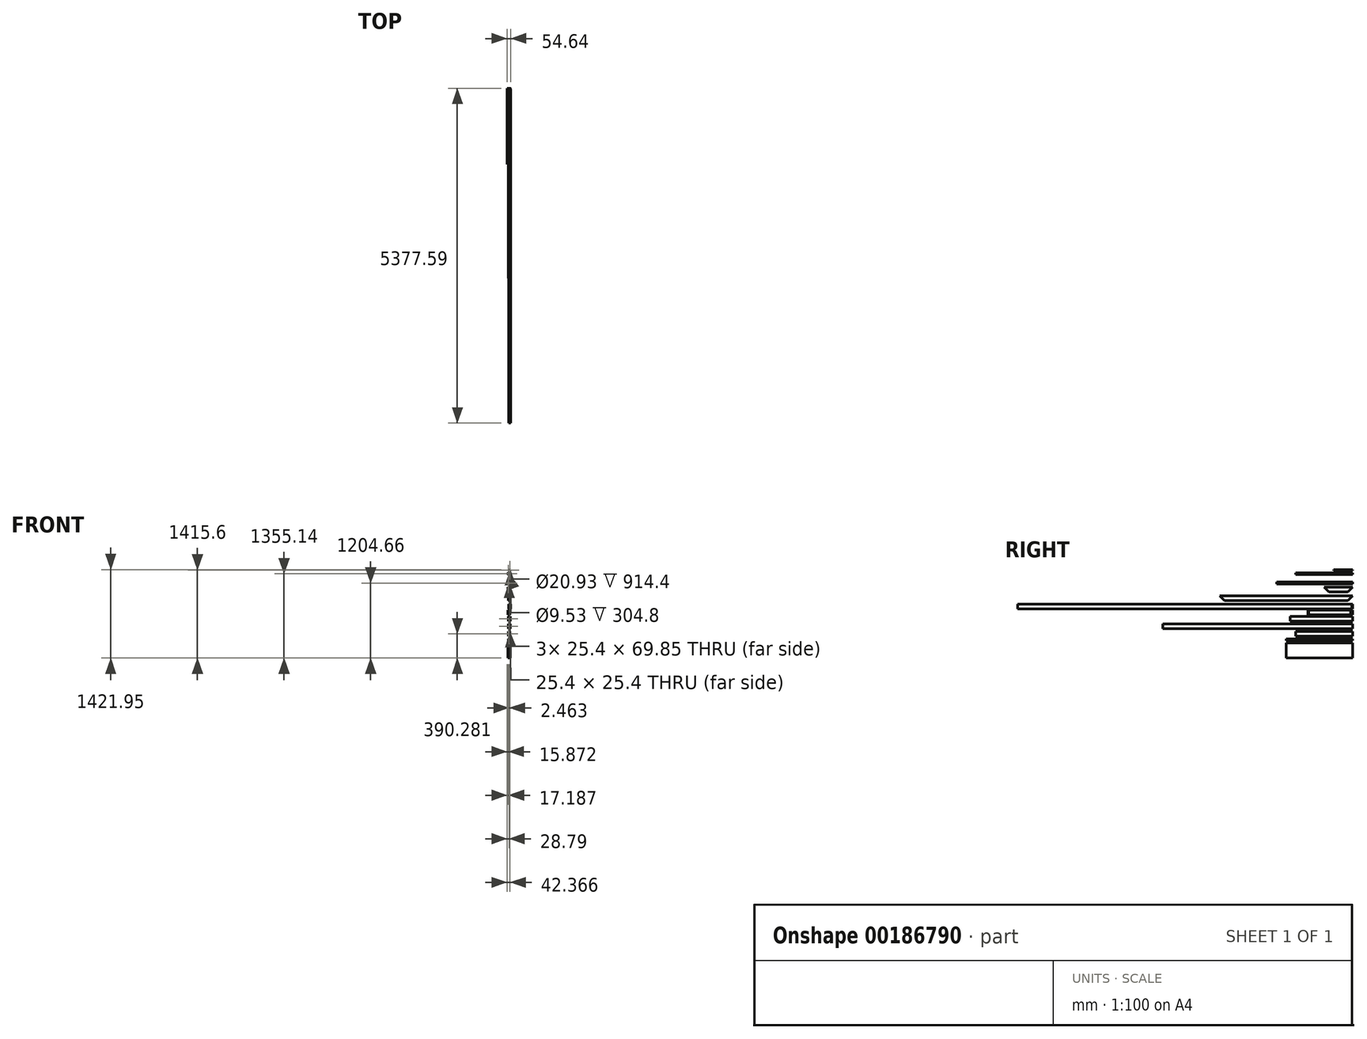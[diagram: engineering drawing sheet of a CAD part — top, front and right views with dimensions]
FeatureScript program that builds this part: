
annotation { "Feature Type Name" : "Feature", "Feature Type Description" : "" }
export const myFeature = defineFeature(function(context is Context, id is Id, definition is map)
    precondition{}
    {
        {
            var Q0;
            Q0=qCreatedBy(makeId("Front.planeOp"),FACE);
            var sketch = newSketch(context, id + "F0", { "sketchPlane" : qUnion([Q0])});
            skLineSegment(sketch, "E0.bottom", {"start": v(-82.17, 96.46) * mm, "end": v(-56.77, 96.46) * mm});
            skLineSegment(sketch, "E0.top", {"start": v(-82.17, 26.61) * mm, "end": v(-56.77, 26.61) * mm});
            skLineSegment(sketch, "E0.left", {"start": v(-82.17, 96.46) * mm, "end": v(-82.17, 26.61) * mm});
            skLineSegment(sketch, "E0.right", {"start": v(-56.77, 96.46) * mm, "end": v(-56.77, 26.61) * mm});
            skLineSegment(sketch, "E1.bottom", {"start": v(-85.35, 99.64) * mm, "end": v(-53.6, 99.64) * mm});
            skLineSegment(sketch, "E1.top", {"start": v(-85.35, 23.44) * mm, "end": v(-53.6, 23.44) * mm});
            skLineSegment(sketch, "E1.left", {"start": v(-85.35, 99.64) * mm, "end": v(-85.35, 23.44) * mm});
            skLineSegment(sketch, "E1.right", {"start": v(-53.6, 99.64) * mm, "end": v(-53.6, 23.44) * mm});
            skLineSegment(sketch, "E2.bottom", {"start": v(-92.32, -2.1) * mm, "end": v(-66.92, -2.1) * mm});
            skLineSegment(sketch, "E2.top", {"start": v(-92.32, -71.95) * mm, "end": v(-66.92, -71.95) * mm});
            skLineSegment(sketch, "E2.left", {"start": v(-92.32, -2.1) * mm, "end": v(-92.32, -71.95) * mm});
            skLineSegment(sketch, "E2.right", {"start": v(-66.92, -2.1) * mm, "end": v(-66.92, -71.95) * mm});
            skLineSegment(sketch, "E3.bottom", {"start": v(-95.5, 1.08) * mm, "end": v(-63.75, 1.08) * mm});
            skLineSegment(sketch, "E3.top", {"start": v(-95.5, -75.12) * mm, "end": v(-63.75, -75.12) * mm});
            skLineSegment(sketch, "E3.left", {"start": v(-95.5, 1.08) * mm, "end": v(-95.5, -75.12) * mm});
            skLineSegment(sketch, "E3.right", {"start": v(-63.75, 1.08) * mm, "end": v(-63.75, -75.12) * mm});
            skLineSegment(sketch, "E4.bottom", {"start": v(-87.37, -104.41) * mm, "end": v(-61.97, -104.41) * mm});
            skLineSegment(sketch, "E4.top", {"start": v(-87.37, -174.26) * mm, "end": v(-61.97, -174.26) * mm});
            skLineSegment(sketch, "E4.left", {"start": v(-87.37, -104.41) * mm, "end": v(-87.37, -174.26) * mm});
            skLineSegment(sketch, "E4.right", {"start": v(-61.97, -104.41) * mm, "end": v(-61.97, -174.26) * mm});
            skLineSegment(sketch, "E5.bottom", {"start": v(-90.55, -101.24) * mm, "end": v(-58.8, -101.24) * mm});
            skLineSegment(sketch, "E5.top", {"start": v(-90.55, -177.44) * mm, "end": v(-58.8, -177.44) * mm});
            skLineSegment(sketch, "E5.left", {"start": v(-90.55, -101.24) * mm, "end": v(-90.55, -177.44) * mm});
            skLineSegment(sketch, "E5.right", {"start": v(-58.8, -101.24) * mm, "end": v(-58.8, -177.44) * mm});
            skLineSegment(sketch, "E6.bottom", {"start": v(-89.69, -223.53) * mm, "end": v(-64.29, -223.53) * mm});
            skLineSegment(sketch, "E6.top", {"start": v(-89.69, -293.38) * mm, "end": v(-64.29, -293.38) * mm});
            skLineSegment(sketch, "E6.left", {"start": v(-89.69, -223.53) * mm, "end": v(-89.69, -293.38) * mm});
            skLineSegment(sketch, "E6.right", {"start": v(-64.29, -223.53) * mm, "end": v(-64.29, -293.38) * mm});
            skLineSegment(sketch, "E7.bottom", {"start": v(-92.86, -220.36) * mm, "end": v(-61.11, -220.36) * mm});
            skLineSegment(sketch, "E7.top", {"start": v(-92.86, -296.56) * mm, "end": v(-61.11, -296.56) * mm});
            skLineSegment(sketch, "E7.left", {"start": v(-92.86, -220.36) * mm, "end": v(-92.86, -296.56) * mm});
            skLineSegment(sketch, "E7.right", {"start": v(-61.11, -220.36) * mm, "end": v(-61.11, -296.56) * mm});
            skLineSegment(sketch, "E8.bottom", {"start": v(-92.15, -344.23) * mm, "end": v(-66.75, -344.23) * mm});
            skLineSegment(sketch, "E8.top", {"start": v(-92.15, -414.08) * mm, "end": v(-66.75, -414.08) * mm});
            skLineSegment(sketch, "E8.left", {"start": v(-92.15, -344.23) * mm, "end": v(-92.15, -414.08) * mm});
            skLineSegment(sketch, "E8.right", {"start": v(-66.75, -344.23) * mm, "end": v(-66.75, -414.08) * mm});
            skLineSegment(sketch, "E9.bottom", {"start": v(-95.33, -341.06) * mm, "end": v(-63.58, -341.06) * mm});
            skLineSegment(sketch, "E9.top", {"start": v(-95.33, -417.26) * mm, "end": v(-63.58, -417.26) * mm});
            skLineSegment(sketch, "E9.left", {"start": v(-95.33, -341.06) * mm, "end": v(-95.33, -417.26) * mm});
            skLineSegment(sketch, "E9.right", {"start": v(-63.58, -341.06) * mm, "end": v(-63.58, -417.26) * mm});
            skLineSegment(sketch, "E10", {"start": v(-95.36, -464.32) * mm, "end": v(-95.36, -489.72) * mm});
            skLineSegment(sketch, "E11", {"start": v(-95.36, -489.72) * mm, "end": v(-69.96, -489.72) * mm});
            skLineSegment(sketch, "E12", {"start": v(-69.96, -489.72) * mm, "end": v(-69.96, -486.54) * mm});
            skLineSegment(sketch, "E13", {"start": v(-69.96, -486.54) * mm, "end": v(-92.19, -486.54) * mm});
            skLineSegment(sketch, "E14", {"start": v(-92.19, -486.54) * mm, "end": v(-92.19, -464.32) * mm});
            skLineSegment(sketch, "E15", {"start": v(-92.19, -464.32) * mm, "end": v(-95.36, -464.32) * mm});
            skLineSegment(sketch, "E16.bottom", {"start": v(-100.1, -528.14) * mm, "end": v(-62, -528.14) * mm});
            skLineSegment(sketch, "E16.top", {"start": v(-100.1, -769.44) * mm, "end": v(-62, -769.44) * mm});
            skLineSegment(sketch, "E16.left", {"start": v(-100.1, -528.14) * mm, "end": v(-100.1, -769.44) * mm});
            skLineSegment(sketch, "E16.right", {"start": v(-62, -528.14) * mm, "end": v(-62, -769.44) * mm});
            skLineSegment(sketch, "E17.bottom", {"start": v(-89.06, 227.94) * mm, "end": v(-63.66, 227.94) * mm});
            skLineSegment(sketch, "E17.top", {"start": v(-89.06, 158.09) * mm, "end": v(-63.66, 158.09) * mm});
            skLineSegment(sketch, "E17.left", {"start": v(-89.06, 227.94) * mm, "end": v(-89.06, 158.09) * mm});
            skLineSegment(sketch, "E17.right", {"start": v(-63.66, 227.94) * mm, "end": v(-63.66, 158.09) * mm});
            skLineSegment(sketch, "E18.bottom", {"start": v(-92.24, 231.11) * mm, "end": v(-60.49, 231.11) * mm});
            skLineSegment(sketch, "E18.top", {"start": v(-92.24, 154.91) * mm, "end": v(-60.49, 154.91) * mm});
            skLineSegment(sketch, "E18.left", {"start": v(-92.24, 231.11) * mm, "end": v(-92.24, 154.91) * mm});
            skLineSegment(sketch, "E18.right", {"start": v(-60.49, 231.11) * mm, "end": v(-60.49, 154.91) * mm});
            skLineSegment(sketch, "E19.bottom", {"start": v(-96.85, 368.67) * mm, "end": v(-71.45, 368.67) * mm});
            skLineSegment(sketch, "E19.top", {"start": v(-96.85, 298.82) * mm, "end": v(-71.45, 298.82) * mm});
            skLineSegment(sketch, "E19.left", {"start": v(-96.85, 368.67) * mm, "end": v(-96.85, 298.82) * mm});
            skLineSegment(sketch, "E19.right", {"start": v(-71.45, 368.67) * mm, "end": v(-71.45, 298.82) * mm});
            skLineSegment(sketch, "E20.bottom", {"start": v(-100.03, 371.84) * mm, "end": v(-68.28, 371.84) * mm});
            skLineSegment(sketch, "E20.top", {"start": v(-100.03, 295.64) * mm, "end": v(-68.28, 295.64) * mm});
            skLineSegment(sketch, "E20.left", {"start": v(-100.03, 371.84) * mm, "end": v(-100.03, 295.64) * mm});
            skLineSegment(sketch, "E20.right", {"start": v(-68.28, 371.84) * mm, "end": v(-68.28, 295.64) * mm});
            skLineSegment(sketch, "E21.bottom", {"start": v(-108.24, 451.1) * mm, "end": v(-76.5, 451.1) * mm});
            skLineSegment(sketch, "E21.top", {"start": v(-108.24, 419.35) * mm, "end": v(-76.5, 419.35) * mm});
            skLineSegment(sketch, "E21.left", {"start": v(-108.24, 451.1) * mm, "end": v(-108.24, 419.35) * mm});
            skLineSegment(sketch, "E21.right", {"start": v(-76.5, 451.1) * mm, "end": v(-76.5, 419.35) * mm});
            skLineSegment(sketch, "E22.bottom", {"start": v(-105.07, 447.93) * mm, "end": v(-79.67, 447.93) * mm});
            skLineSegment(sketch, "E22.top", {"start": v(-105.07, 422.53) * mm, "end": v(-79.67, 422.53) * mm});
            skLineSegment(sketch, "E22.left", {"start": v(-105.07, 447.93) * mm, "end": v(-105.07, 422.53) * mm});
            skLineSegment(sketch, "E22.right", {"start": v(-79.67, 447.93) * mm, "end": v(-79.67, 422.53) * mm});
            skCircle(sketch, "E23", {"center": v(-65.87, 646.16) * mm, "radius": 6.35 * mm});
            skCircle(sketch, "E24", {"center": v(-65.87, 646.16) * mm, "radius": 4.76 * mm});
            skCircle(sketch, "E25", {"center": v(-91.05, 585.7) * mm, "radius": 13.33 * mm});
            skCircle(sketch, "E26", {"center": v(-91.05, 585.7) * mm, "radius": 10.46 * mm});
            skSolve(sketch);
        }
        {
            var Q0;
            Q0=makeQuery(id+"F0.imprint","IMPRINT",FACE,{"disambiguationData":[TD([[makeQuery(id+"F0.imprint","IMPRINT",EDGE,{"derivedFrom":sQuery(id+"F0.wireOp",EDGE,"E0.bottom")}),1.0]])]});
            extrude(context, id + "F1", {"entities" : qUnion([Q0]), "depth" : 5377.59 * mm});
        }
        {
            var Q0;
            Q0=makeQuery(id+"F0.imprint","IMPRINT",FACE,{"disambiguationData":[TD([[makeQuery(id+"F0.imprint","IMPRINT",EDGE,{"derivedFrom":sQuery(id+"F0.wireOp",EDGE,"E2.bottom")}),1.0]])]});
            extrude(context, id + "F2", {"entities" : qUnion([Q0]), "depth" : 718.4 * mm});
        }
        {
            var Q0;
            Q0=makeQuery(id+"F0.imprint","IMPRINT",FACE,{"disambiguationData":[TD([[makeQuery(id+"F0.imprint","IMPRINT",EDGE,{"derivedFrom":sQuery(id+"F0.wireOp",EDGE,"E4.bottom")}),1.0]])]});
            extrude(context, id + "F3", {"entities" : qUnion([Q0]), "depth" : 1003.3 * mm});
        }
        {
            var Q0;
            Q0=makeQuery(id+"F0.imprint","IMPRINT",FACE,{"disambiguationData":[TD([[makeQuery(id+"F0.imprint","IMPRINT",EDGE,{"derivedFrom":sQuery(id+"F0.wireOp",EDGE,"E6.bottom")}),1.0]])]});
            extrude(context, id + "F4", {"entities" : qUnion([Q0]), "depth" : 3048 * mm});
        }
        {
            var Q0;
            Q0=makeQuery(id+"F1.opExtrude","SWEPT_FACE",FACE,{"disambiguationData":[OSD([sQuery(id+"F0.wireOp",EDGE,"E1.bottom")])]});
            var sketch = newSketch(context, id + "F5", { "sketchPlane" : qUnion([Q0])});
            skLineSegment(sketch, "E27", {"start": v(-85.35, 0) * mm, "end": v(-53.6, -13.15) * mm});
            skLineSegment(sketch, "E28", {"start": v(-53.6, -13.15) * mm, "end": v(-53.6, 0) * mm});
            skLineSegment(sketch, "E29", {"start": v(-53.6, 0) * mm, "end": v(-85.35, 0) * mm});
            skSolve(sketch);
        }
        {
            var Q0;
            Q0=makeQuery(id+"F5.imprint","IMPRINT",FACE,{"disambiguationData":[TD([[makeQuery(id+"F5.imprint","IMPRINT",EDGE,{"derivedFrom":sQuery(id+"F5.wireOp",EDGE,"E27")}),1.0]])]});
            extrude(context, id + "F6", {"entities" : qUnion([Q0]), "operationType" : NewBodyOperationType.REMOVE, "oppositeDirection" : true, "depth" : 76.2 * mm});
        }
        {
            var Q0;
            Q0=makeQuery(id+"F2.opExtrude","SWEPT_FACE",FACE,{"disambiguationData":[OSD([sQuery(id+"F0.wireOp",EDGE,"E3.bottom")])]});
            var sketch = newSketch(context, id + "F7", { "sketchPlane" : qUnion([Q0])});
            skLineSegment(sketch, "E30", {"start": v(-95.5, 0) * mm, "end": v(-63.75, 0) * mm});
            skLineSegment(sketch, "E31", {"start": v(-63.75, 0) * mm, "end": v(-63.75, -31.75) * mm});
            skLineSegment(sketch, "E32", {"start": v(-63.75, -31.75) * mm, "end": v(-95.5, 0) * mm});
            skLineSegment(sketch, "E33", {"start": v(-95.5, -718.41) * mm, "end": v(-63.75, -718.41) * mm});
            skLineSegment(sketch, "E34", {"start": v(-63.75, -718.41) * mm, "end": v(-63.75, -705.26) * mm});
            skLineSegment(sketch, "E35", {"start": v(-63.75, -705.26) * mm, "end": v(-95.5, -718.41) * mm});
            skSolve(sketch);
        }
        {
            var Q0;
            Q0=makeQuery(id+"F7.imprint","IMPRINT",FACE,{"disambiguationData":[TD([[makeQuery(id+"F7.imprint","IMPRINT",EDGE,{"derivedFrom":sQuery(id+"F7.wireOp",EDGE,"E30")}),-1.0]])]});
            var Q1;
            Q1=makeQuery(id+"F7.imprint","IMPRINT",FACE,{"disambiguationData":[TD([[makeQuery(id+"F7.imprint","IMPRINT",EDGE,{"derivedFrom":sQuery(id+"F7.wireOp",EDGE,"E33")}),1.0]])]});
            extrude(context, id + "F8", {"entities" : qUnion([Q0, Q1]), "operationType" : NewBodyOperationType.REMOVE, "oppositeDirection" : true, "depth" : 76.2 * mm});
        }
        {
            var Q0;
            Q0=makeQuery(id+"F0.imprint","IMPRINT",FACE,{"disambiguationData":[TD([[makeQuery(id+"F0.imprint","IMPRINT",EDGE,{"derivedFrom":sQuery(id+"F0.wireOp",EDGE,"E10")}),1.0]])]});
            extrude(context, id + "F9", {"entities" : qUnion([Q0]), "depth" : 1066.8 * mm});
        }
        {
            var Q0;
            Q0=makeQuery(id+"F0.imprint","IMPRINT",FACE,{"disambiguationData":[TD([[makeQuery(id+"F0.imprint","IMPRINT",EDGE,{"derivedFrom":sQuery(id+"F0.wireOp",EDGE,"E16.bottom")}),-1.0]])]});
            var Q1;
            Q1=makeQuery(id+"F9.opExtrude","CAP_FACE",FACE,{"disambiguationData":[OSD([sQuery(id+"F0.wireOp",EDGE,"E10"),sQuery(id+"F0.wireOp",EDGE,"E11"),sQuery(id+"F0.wireOp",EDGE,"E12"),sQuery(id+"F0.wireOp",EDGE,"E13"),sQuery(id+"F0.wireOp",EDGE,"E14"),sQuery(id+"F0.wireOp",EDGE,"E15")])],"isStart":false});
            extrude(context, id + "F10", {"entities" : qUnion([Q0]), "endBound" : BoundingType.UP_TO_SURFACE, "endBoundEntityFace" : qUnion([Q1]), "depth" : 25.4 * mm});
        }
        {
            var Q0;
            Q0=makeQuery(id+"F0.imprint","IMPRINT",FACE,{"disambiguationData":[TD([[makeQuery(id+"F0.imprint","IMPRINT",EDGE,{"derivedFrom":sQuery(id+"F0.wireOp",EDGE,"E17.bottom")}),1.0]])]});
            extrude(context, id + "F11", {"entities" : qUnion([Q0]), "depth" : 2133.6 * mm});
        }
        {
            var Q0;
            Q0=makeQuery(id+"F11.opExtrude","SWEPT_FACE",FACE,{"disambiguationData":[OSD([sQuery(id+"F0.wireOp",EDGE,"E18.right")])]});
            var sketch = newSketch(context, id + "F12", { "sketchPlane" : qUnion([Q0])});
            skLineSegment(sketch, "E36", {"start": v(0, 231.11) * mm, "end": v(0, 154.91) * mm});
            skLineSegment(sketch, "E37", {"start": v(0, 154.91) * mm, "end": v(-76.2, 154.91) * mm});
            skLineSegment(sketch, "E38", {"start": v(-76.2, 154.91) * mm, "end": v(0, 231.11) * mm});
            skLineSegment(sketch, "E39", {"start": v(-2133.6, 231.11) * mm, "end": v(-2133.6, 154.91) * mm});
            skLineSegment(sketch, "E40", {"start": v(-2133.6, 154.91) * mm, "end": v(-2057.4, 154.91) * mm});
            skLineSegment(sketch, "E41", {"start": v(-2057.4, 154.91) * mm, "end": v(-2133.6, 231.11) * mm});
            skSolve(sketch);
        }
        {
            var Q0;
            Q0=makeQuery(id+"F12.imprint","IMPRINT",FACE,{"disambiguationData":[TD([[makeQuery(id+"F12.imprint","IMPRINT",EDGE,{"derivedFrom":sQuery(id+"F12.wireOp",EDGE,"E36")}),-1.0]])]});
            var Q1;
            Q1=makeQuery(id+"F12.imprint","IMPRINT",FACE,{"disambiguationData":[TD([[makeQuery(id+"F12.imprint","IMPRINT",EDGE,{"derivedFrom":sQuery(id+"F12.wireOp",EDGE,"E39")}),1.0]])]});
            extrude(context, id + "F13", {"entities" : qUnion([Q0, Q1]), "operationType" : NewBodyOperationType.REMOVE, "oppositeDirection" : true, "depth" : 31.75 * mm});
        }
        {
            var Q0;
            Q0=makeQuery(id+"F0.imprint","IMPRINT",FACE,{"disambiguationData":[TD([[makeQuery(id+"F0.imprint","IMPRINT",EDGE,{"derivedFrom":sQuery(id+"F0.wireOp",EDGE,"E8.bottom")}),1.0]])]});
            extrude(context, id + "F14", {"entities" : qUnion([Q0]), "depth" : 914.4 * mm});
        }
        {
            var Q0;
            Q0=makeQuery(id+"F0.imprint","IMPRINT",FACE,{"disambiguationData":[TD([[makeQuery(id+"F0.imprint","IMPRINT",EDGE,{"derivedFrom":sQuery(id+"F0.wireOp",EDGE,"E19.bottom")}),1.0]])]});
            extrude(context, id + "F15", {"entities" : qUnion([Q0]), "depth" : 457.2 * mm});
        }
        {
            var Q0;
            Q0=makeQuery(id+"F15.opExtrude","SWEPT_FACE",FACE,{"disambiguationData":[OSD([sQuery(id+"F0.wireOp",EDGE,"E20.right")])]});
            var sketch = newSketch(context, id + "F16", { "sketchPlane" : qUnion([Q0])});
            skLineSegment(sketch, "E42", {"start": v(-457.2, 371.84) * mm, "end": v(-457.2, 295.64) * mm});
            skLineSegment(sketch, "E43", {"start": v(-457.2, 295.64) * mm, "end": v(-381, 295.64) * mm});
            skLineSegment(sketch, "E44", {"start": v(-381, 295.64) * mm, "end": v(-457.2, 371.84) * mm});
            skLineSegment(sketch, "E45", {"start": v(0, 371.84) * mm, "end": v(-76.2, 295.64) * mm});
            skLineSegment(sketch, "E46", {"start": v(-76.2, 295.64) * mm, "end": v(0, 295.64) * mm});
            skLineSegment(sketch, "E47", {"start": v(0, 295.64) * mm, "end": v(0, 371.84) * mm});
            skSolve(sketch);
        }
        {
            var Q0;
            Q0=makeQuery(id+"F16.imprint","IMPRINT",FACE,{"disambiguationData":[TD([[makeQuery(id+"F16.imprint","IMPRINT",EDGE,{"derivedFrom":sQuery(id+"F16.wireOp",EDGE,"E42")}),1.0]])]});
            var Q1;
            Q1=makeQuery(id+"F16.imprint","IMPRINT",FACE,{"disambiguationData":[TD([[makeQuery(id+"F16.imprint","IMPRINT",EDGE,{"derivedFrom":sQuery(id+"F16.wireOp",EDGE,"E45")}),1.0]])]});
            extrude(context, id + "F17", {"entities" : qUnion([Q0, Q1]), "operationType" : NewBodyOperationType.REMOVE, "oppositeDirection" : true, "depth" : 31.75 * mm});
        }
        {
            var Q0;
            Q0=makeQuery(id+"F0.imprint","IMPRINT",FACE,{"disambiguationData":[TD([[makeQuery(id+"F0.imprint","IMPRINT",EDGE,{"derivedFrom":sQuery(id+"F0.wireOp",EDGE,"E21.bottom")}),-1.0]])]});
            extrude(context, id + "F18", {"entities" : qUnion([Q0]), "depth" : 1219.2 * mm});
        }
        {
            var Q0;
            Q0=makeQuery(id+"F0.imprint","IMPRINT",FACE,{"disambiguationData":[TD([[makeQuery(id+"F0.imprint","IMPRINT",EDGE,{"derivedFrom":sQuery(id+"F0.wireOp",EDGE,"E23")}),1.0]])]});
            extrude(context, id + "F19", {"entities" : qUnion([Q0]), "depth" : 304.8 * mm});
        }
        {
            var Q0;
            Q0=makeQuery(id+"F0.imprint","IMPRINT",FACE,{"disambiguationData":[TD([[makeQuery(id+"F0.imprint","IMPRINT",EDGE,{"derivedFrom":sQuery(id+"F0.wireOp",EDGE,"E25")}),1.0]])]});
            extrude(context, id + "F20", {"entities" : qUnion([Q0]), "depth" : 914.4 * mm});
        }
    });
